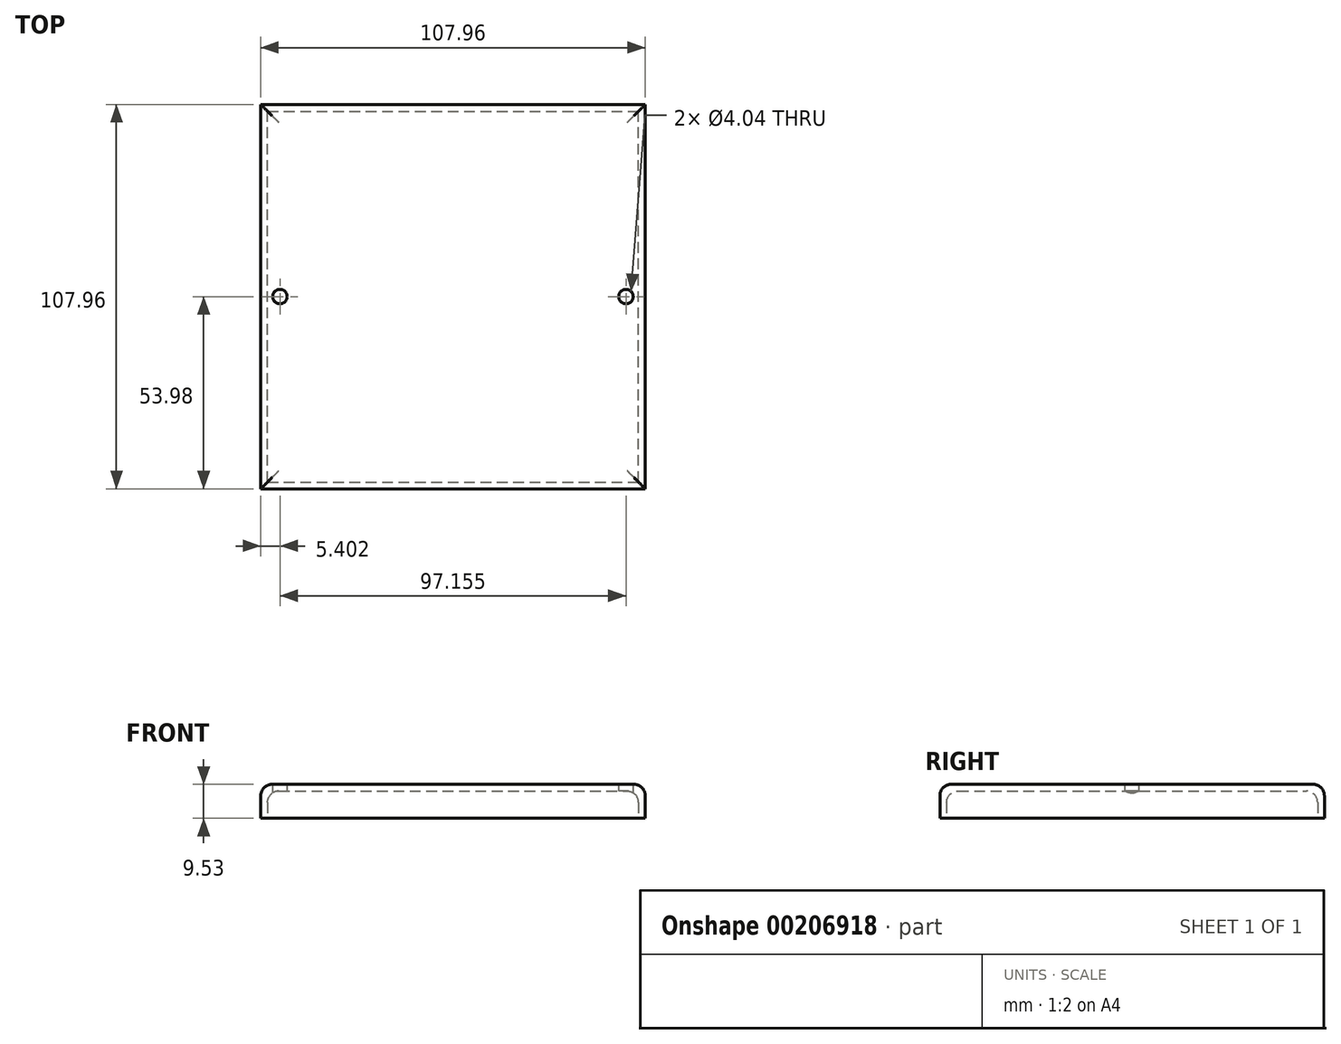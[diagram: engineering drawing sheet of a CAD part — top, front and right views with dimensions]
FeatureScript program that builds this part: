
annotation { "Feature Type Name" : "Feature", "Feature Type Description" : "" }
export const myFeature = defineFeature(function(context is Context, id is Id, definition is map)
    precondition{}
    {
        {
            var Q0;
            Q0=qCreatedBy(makeId("Top.planeOp"),FACE);
            var sketch = newSketch(context, id + "F0", { "sketchPlane" : qUnion([Q0])});
            skLineSegment(sketch, "E0.bottom", {"start": v(-53.97, 53.98) * mm, "end": v(53.98, 53.98) * mm});
            skLineSegment(sketch, "E0.top", {"start": v(-53.98, -53.98) * mm, "end": v(53.97, -53.98) * mm});
            skLineSegment(sketch, "E0.left", {"start": v(-53.97, 53.98) * mm, "end": v(-53.98, -53.98) * mm});
            skLineSegment(sketch, "E0.right", {"start": v(53.98, 53.98) * mm, "end": v(53.97, -53.98) * mm});
            skPoint(sketch, "E0.middle", {"position": v(0, 0) * mm});
            skSolve(sketch);
        }
        {
            var Q0;
            Q0=qSketchRegion(id+"F0",true);
            extrude(context, id + "F1", {"entities" : qUnion([Q0]), "depth" : 9.52 * mm});
        }
        {
            var Q0;
            Q0=makeQuery(id+"F1.opExtrude","CAP_FACE",FACE,{"disambiguationData":[OSD([sQuery(id+"F0.wireOp",EDGE,"E0.bottom"),sQuery(id+"F0.wireOp",EDGE,"E0.top"),sQuery(id+"F0.wireOp",EDGE,"E0.left"),sQuery(id+"F0.wireOp",EDGE,"E0.right")])],"isStart":true});
            var sketch = newSketch(context, id + "F2", { "sketchPlane" : qUnion([Q0])});
            skLineSegment(sketch, "E1.bottom", {"start": v(-52.08, 52.08) * mm, "end": v(52.08, 52.08) * mm});
            skLineSegment(sketch, "E1.top", {"start": v(-52.08, -52.08) * mm, "end": v(52.08, -52.08) * mm});
            skLineSegment(sketch, "E1.left", {"start": v(-52.08, 52.08) * mm, "end": v(-52.08, -52.08) * mm});
            skLineSegment(sketch, "E1.right", {"start": v(52.08, 52.08) * mm, "end": v(52.08, -52.08) * mm});
            skPoint(sketch, "E1.middle", {"position": v(0, 0) * mm});
            skSolve(sketch);
        }
        {
            var Q0;
            Q0=qSketchRegion(id+"F2",true);
            extrude(context, id + "F3", {"entities" : qUnion([Q0]), "operationType" : NewBodyOperationType.REMOVE, "oppositeDirection" : true, "depth" : 7.63 * mm});
        }
        {
            var Q0;
            Q0=makeQuery(id+"F3.boolean.opBoolean","COPY",FACE,{"derivedFrom":makeQuery(id+"F3.opExtrude","CAP_FACE",FACE,{"disambiguationData":[OSD([sQuery(id+"F2.wireOp",EDGE,"E1.bottom"),sQuery(id+"F2.wireOp",EDGE,"E1.top"),sQuery(id+"F2.wireOp",EDGE,"E1.left"),sQuery(id+"F2.wireOp",EDGE,"E1.right")])],"isStart":false})});
            var Q1;
            Q1=makeQuery(id+"F1.opExtrude","CAP_FACE",FACE,{"disambiguationData":[OSD([sQuery(id+"F0.wireOp",EDGE,"E0.bottom"),sQuery(id+"F0.wireOp",EDGE,"E0.top"),sQuery(id+"F0.wireOp",EDGE,"E0.left"),sQuery(id+"F0.wireOp",EDGE,"E0.right")])],"isStart":false});
            fillet(context, id + "F4", {"entities" : qUnion([Q0, Q1]), "radius" : 3.17 * mm, "tangentPropagation" : true, "allowEdgeOverflow" : false});
        }
        {
            var Q0;
            Q0=makeQuery(id+"F1.opExtrude","CAP_FACE",FACE,{"disambiguationData":[OSD([sQuery(id+"F0.wireOp",EDGE,"E0.bottom"),sQuery(id+"F0.wireOp",EDGE,"E0.top"),sQuery(id+"F0.wireOp",EDGE,"E0.left"),sQuery(id+"F0.wireOp",EDGE,"E0.right")])],"isStart":false});
            var sketch = newSketch(context, id + "F5", { "sketchPlane" : qUnion([Q0])});
            skPoint(sketch, "E2", {"position": v(-48.58, 0) * mm});
            skPoint(sketch, "E3", {"position": v(48.58, 0) * mm});
            skSolve(sketch);
        }
        {
            var Q0;
            Q0=sQuery(id+"F5.wireOp",VERTEX,"E2");
            var Q1;
            Q1=sQuery(id+"F5.wireOp",VERTEX,"E3");
            var Q2;
            Q2=makeQuery(id+"F1.opExtrude","SWEPT_BODY",BODY,{"disambiguationData":[OSD([sQuery(id+"F0.wireOp",EDGE,"E0.bottom"),sQuery(id+"F0.wireOp",EDGE,"E0.top"),sQuery(id+"F0.wireOp",EDGE,"E0.left"),sQuery(id+"F0.wireOp",EDGE,"E0.right")])]});
            hole(context, id + "F6", {"style" : HoleStyle.SIMPLE, "endStyle" : HoleEndStyle.BLIND, "standardTappedOrClearance" : lookupTablePath({ "standard" : "ANSI", "engagement" : "75%", "pitch" : "32 tpi", "size" : "#10", "type" : "Tapped" }), "standardBlindInLast" : lookupTablePath({ "standard" : "ANSI", "engagement" : "75%", "pitch" : "32 tpi", "size" : "#10", "type" : "Tapped" }), "holeDiameter" : 4.04 * mm, "holeDepth" : 8.9 * mm, "locations" : qUnion([Q0, Q1]), "scope" : qUnion([Q2]), "majorDiameter" : 4.83 * mm});
        }
    });
